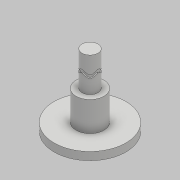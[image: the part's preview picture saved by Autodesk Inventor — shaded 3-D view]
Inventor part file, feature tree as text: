
AUTODESK INVENTOR PART (.ipt)
format: ipt  version: 2018 (Build 220112000, 112)  size: 752,128 bytes
history: native  units: mm
features: other x22, sketch x6, pattern_linear x1
ambient origin geometry x8: Origin, YZ Plane, XZ Plane, XY Plane, X Axis, Y Axis, Z Axis, Center Point
bodies: Body1 (feature_tree), Body2 (feature_tree), Body3 (feature_tree), Body4 (feature_tree), Body5 (feature_tree)
feature tree (29):
  other  "實體1"
  sketch  "3D 草圖1"
  pattern_linear  "矩形陣列1"  Count1=360 Spacing1=0.0mm
  other  "迴轉1"
  other  "分割7"
  other  "分割9"
  other  "增厚9"
  other  "迴轉2"
  other  "分割10"
  other  "分割11"
  sketch  "3D 草圖4"
  other  "分割12"
  other  "分割13"
  other  "增厚11"
  sketch  "3D 草圖2"
  sketch  "3D 草圖3"
  other  "3D 方程式曲線1"
  sketch  "草圖1"
  sketch  "草圖2"
  other  "Srf2"
  other  "Srf3"
  other  "Srf4"
  other  "Srf5"
  other  "投影至曲面1"
  other  "投影至曲面2"
  other  "邊界補面1"
  other  "邊界補面2"
  other  "邊界補面3"
  other  "邊界補面4"
